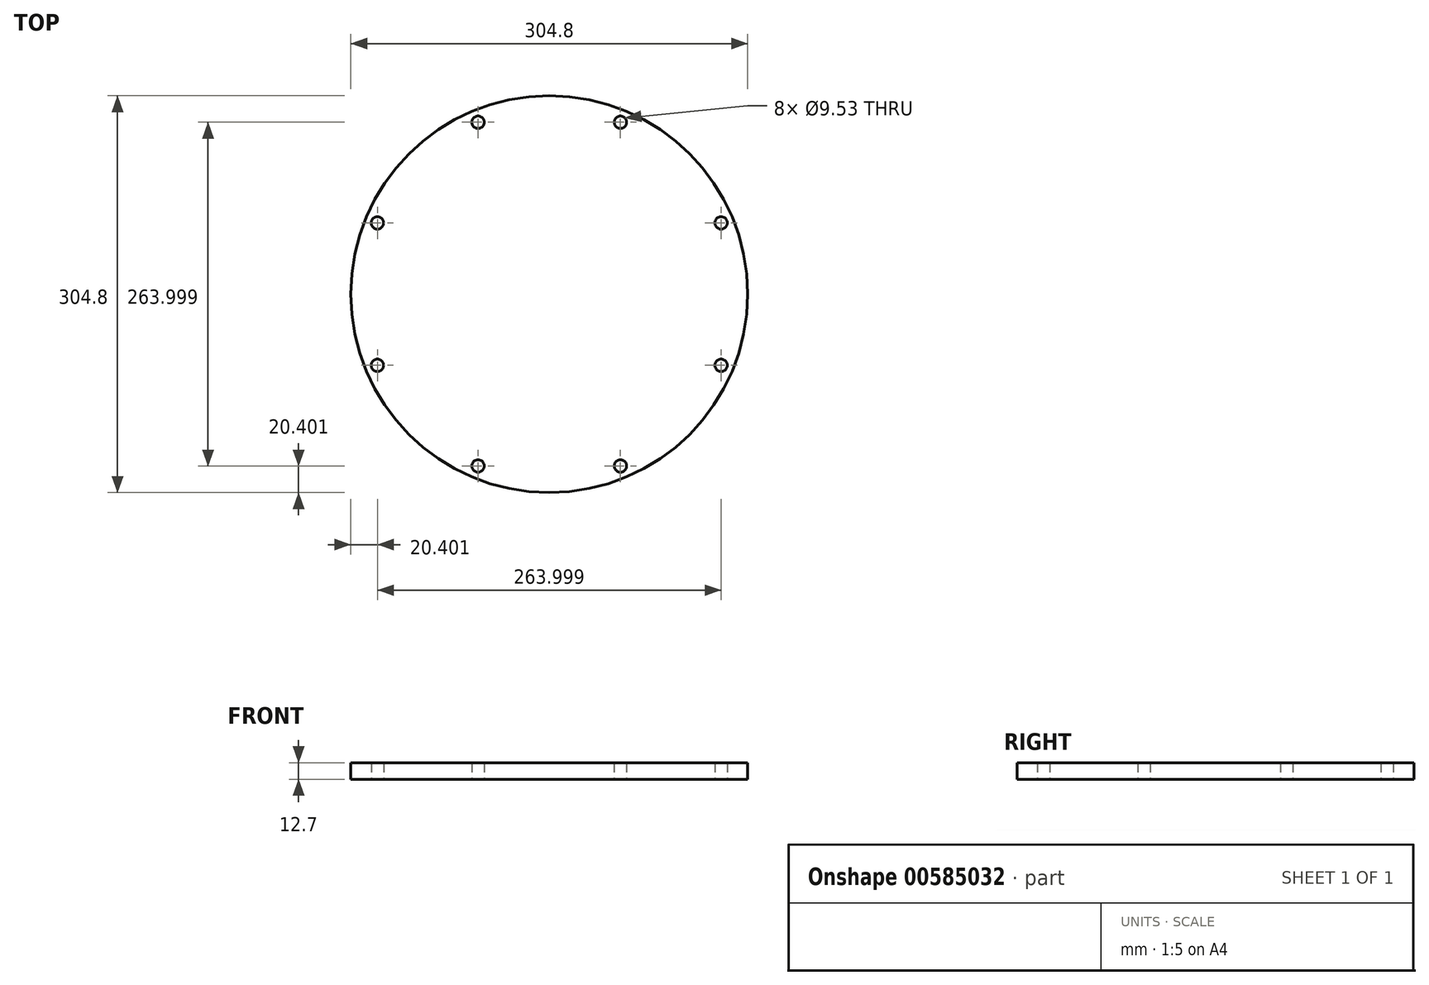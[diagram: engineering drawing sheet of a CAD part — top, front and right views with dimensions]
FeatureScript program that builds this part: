
annotation { "Feature Type Name" : "Feature", "Feature Type Description" : "" }
export const myFeature = defineFeature(function(context is Context, id is Id, definition is map)
    precondition{}
    {
        {
            var Q0;
            Q0=qCreatedBy(makeId("Top.planeOp"),FACE);
            var sketch = newSketch(context, id + "F0", { "sketchPlane" : qUnion([Q0])});
            skCircle(sketch, "E0", {"center": v(0, 0) * mm, "radius": 152.4 * mm});
            skCircle(sketch, "E1", {"center": v(0, 0) * mm, "radius": 142.88 * mm, "construction": true});
            skCircle(sketch, "E2", {"center": v(54.68, 132) * mm, "radius": 4.76 * mm});
            skCircle(sketch, "E3.1.0", {"center": v(-54.68, 132) * mm, "radius": 4.76 * mm});
            skCircle(sketch, "E3.2.0", {"center": v(-132, 54.68) * mm, "radius": 4.76 * mm});
            skCircle(sketch, "E3.3.0", {"center": v(-132, -54.68) * mm, "radius": 4.76 * mm});
            skCircle(sketch, "E3.4.0", {"center": v(-54.68, -132) * mm, "radius": 4.76 * mm});
            skCircle(sketch, "E3.5.0", {"center": v(54.68, -132) * mm, "radius": 4.76 * mm});
            skCircle(sketch, "E3.6.0", {"center": v(132, -54.68) * mm, "radius": 4.76 * mm});
            skCircle(sketch, "E3.7.0", {"center": v(132, 54.68) * mm, "radius": 4.76 * mm});
            skSolve(sketch);
        }
        {
            var Q0;
            Q0 = qSketchRegion(id + "F0", true);
            extrude(context, id + "F1", {"entities" : qUnion([Q0]), "depth" : 12.7 * mm, "offsetDistance" : 25.4 * mm});
        }
    });
